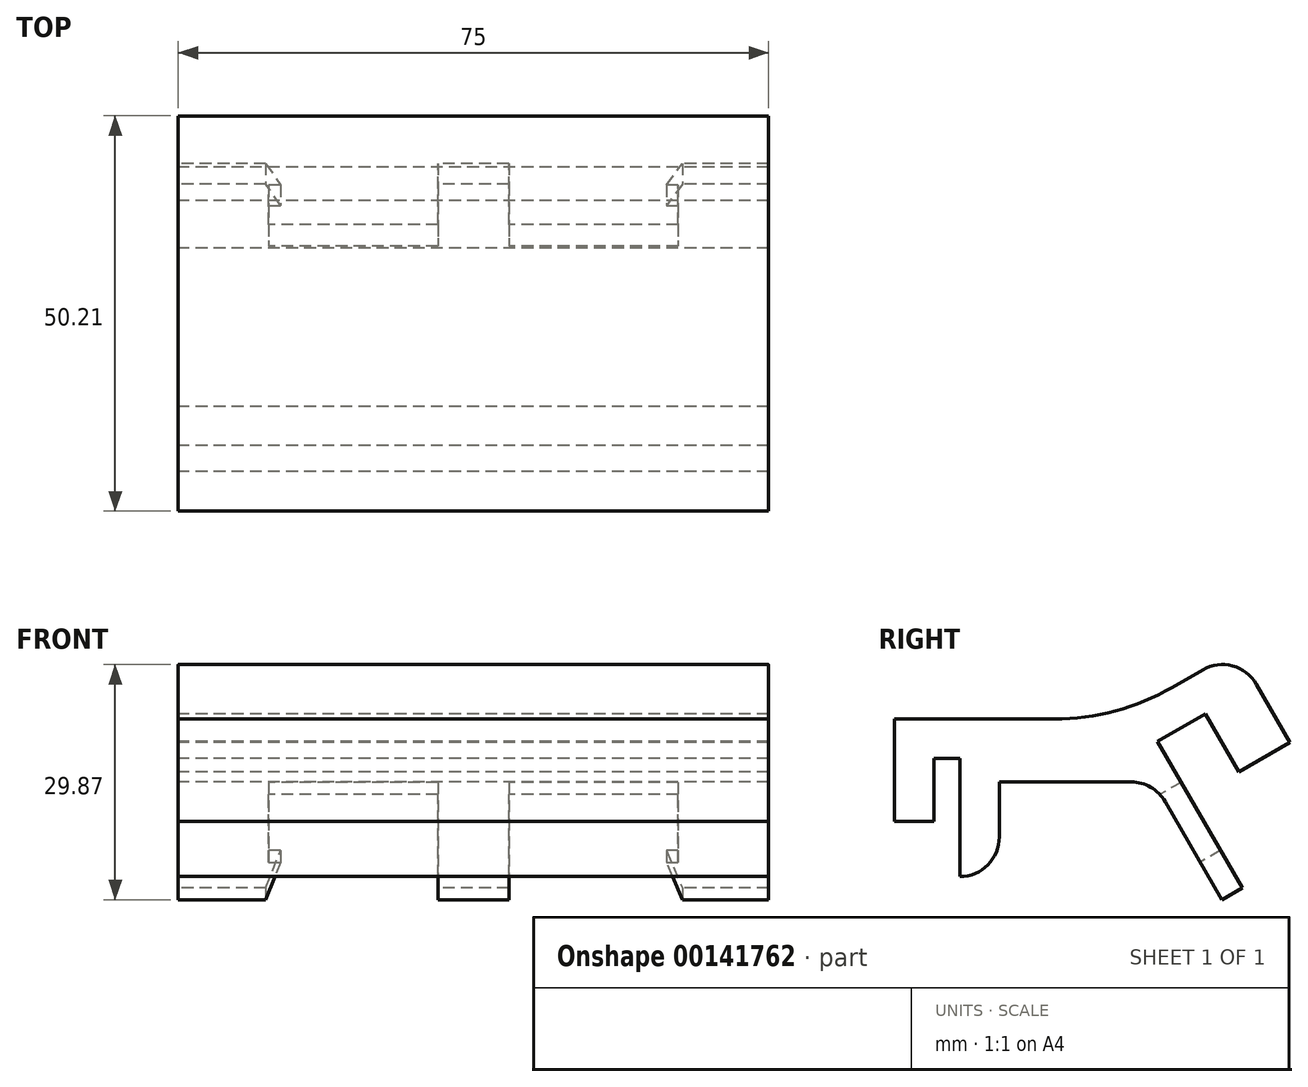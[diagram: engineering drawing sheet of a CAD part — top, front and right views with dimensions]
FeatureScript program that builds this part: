
annotation { "Feature Type Name" : "Feature", "Feature Type Description" : "" }
export const myFeature = defineFeature(function(context is Context, id is Id, definition is map)
    precondition{}
    {
        {
            var Q0;
            Q0=qCreatedBy(makeId("Right.planeOp"),FACE);
            var sketch = newSketch(context, id + "F0", { "sketchPlane" : qUnion([Q0])});
            skLineSegment(sketch, "E0.top", {"start": v(0, 13.5) * mm, "end": v(3, 13.5) * mm});
            skLineSegment(sketch, "E0.left", {"start": v(0, -13) * mm, "end": v(0, 13.5) * mm});
            skLineSegment(sketch, "E0.right", {"start": v(3, -13) * mm, "end": v(3, 8.5) * mm});
            skLineSegment(sketch, "E1.bottom", {"start": v(3, 13.5) * mm, "end": v(10, 13.5) * mm});
            skLineSegment(sketch, "E1.top", {"start": v(3, 8.5) * mm, "end": v(10, 8.5) * mm});
            skLineSegment(sketch, "E2.bottom", {"start": v(10, 13.5) * mm, "end": v(17.5, 13.5) * mm});
            skLineSegment(sketch, "E2.top", {"start": v(10, 0) * mm, "end": v(17.5, 0) * mm});
            skLineSegment(sketch, "E2.left", {"start": v(10, 8.5) * mm, "end": v(10, 0) * mm});
            skLineSegment(sketch, "E2.right", {"start": v(17.5, 13.5) * mm, "end": v(17.5, 0) * mm});
            skLineSegment(sketch, "E3.bottom", {"start": v(-42.45, 43.54) * mm, "end": v(-37.45, 43.54) * mm});
            skLineSegment(sketch, "E3.top", {"start": v(-42.45, 30.54) * mm, "end": v(-37.45, 30.54) * mm});
            skLineSegment(sketch, "E3.left", {"start": v(-42.45, 43.54) * mm, "end": v(-42.45, 30.54) * mm});
            skLineSegment(sketch, "E3.right", {"start": v(-37.45, 43.54) * mm, "end": v(-37.45, 30.54) * mm});
            skLineSegment(sketch, "E4.bottom", {"start": v(-37.45, 43.54) * mm, "end": v(-34.15, 43.54) * mm});
            skLineSegment(sketch, "E4.top", {"start": v(-37.45, 38.54) * mm, "end": v(-34.15, 38.54) * mm});
            skLineSegment(sketch, "E4.left", {"start": v(-37.45, 43.54) * mm, "end": v(-37.45, 38.54) * mm});
            skLineSegment(sketch, "E4.right", {"start": v(-34.15, 43.54) * mm, "end": v(-34.15, 38.54) * mm});
            skLineSegment(sketch, "E5.bottom", {"start": v(-34.15, 43.54) * mm, "end": v(-29.15, 43.54) * mm});
            skLineSegment(sketch, "E5.top", {"start": v(-34.15, 23.54) * mm, "end": v(-29.15, 23.54) * mm});
            skLineSegment(sketch, "E5.left", {"start": v(-34.15, 43.54) * mm, "end": v(-34.15, 23.54) * mm});
            skLineSegment(sketch, "E5.right", {"start": v(-29.15, 43.54) * mm, "end": v(-29.15, 23.54) * mm});
            skLineSegment(sketch, "E6", {"start": v(0, -13) * mm, "end": v(3, -13) * mm});
            skSolve(sketch);
        }
        {
            var Q0;
            Q0=makeQuery(id+"F0.imprint","IMPRINT",FACE,{"disambiguationData":[TD([[makeQuery(id+"F0.imprint","IMPRINT",EDGE,{"derivedFrom":sQuery(id+"F0.wireOp",EDGE,"E0.top")}),-1.0]])]});
            extrude(context, id + "F1", {"entities" : qUnion([Q0]), "depth" : 75 * mm});
        }
        {
            var Q0;
            Q0=qCreatedBy(makeId("Right.planeOp"),FACE);
            var sketch = newSketch(context, id + "F2", { "sketchPlane" : qUnion([Q0])});
            skLineSegment(sketch, "E7.bottom", {"start": v(-28.3, 13.5) * mm, "end": v(-23.3, 13.5) * mm});
            skLineSegment(sketch, "E7.top", {"start": v(-28.3, 0.5) * mm, "end": v(-23.3, 0.5) * mm});
            skLineSegment(sketch, "E7.left", {"start": v(-28.3, 13.5) * mm, "end": v(-28.3, 0.5) * mm});
            skLineSegment(sketch, "E7.right", {"start": v(-23.3, 13.5) * mm, "end": v(-23.3, 0.5) * mm});
            skLineSegment(sketch, "E8.bottom", {"start": v(-23.3, 13.5) * mm, "end": v(-20, 13.5) * mm});
            skLineSegment(sketch, "E8.top", {"start": v(-23.3, 8.5) * mm, "end": v(-20, 8.5) * mm});
            skLineSegment(sketch, "E8.left", {"start": v(-23.3, 13.5) * mm, "end": v(-23.3, 8.5) * mm});
            skLineSegment(sketch, "E8.right", {"start": v(-20, 13.5) * mm, "end": v(-20, 8.5) * mm});
            skLineSegment(sketch, "E9.bottom", {"start": v(-20, 13.5) * mm, "end": v(-15, 13.5) * mm});
            skLineSegment(sketch, "E9.top", {"start": v(-20, -6.5) * mm, "end": v(-15, -6.5) * mm});
            skLineSegment(sketch, "E9.left", {"start": v(-20, 13.5) * mm, "end": v(-20, -6.5) * mm});
            skLineSegment(sketch, "E9.right", {"start": v(-15, 13.5) * mm, "end": v(-15, -6.5) * mm});
            skSolve(sketch);
        }
        {
            var Q0;
            Q0 = qSketchRegion(id + "F2", true);
            extrude(context, id + "F3", {"entities" : qUnion([Q0]), "depth" : 75 * mm});
        }
        {
            var Q0;
            Q0=qCreatedBy(makeId("Front.planeOp"),FACE);
            var sketch = newSketch(context, id + "F4", { "sketchPlane" : qUnion([Q0])});
            skLineSegment(sketch, "E10.bottom", {"start": v(11.5, -7.5) * mm, "end": v(13, -7.5) * mm});
            skLineSegment(sketch, "E10.top", {"start": v(11.5, 2.5) * mm, "end": v(33, 2.5) * mm});
            skLineSegment(sketch, "E10.left", {"start": v(11.5, -7.5) * mm, "end": v(11.5, 2.5) * mm});
            skLineSegment(sketch, "E10.right", {"start": v(33, -7.5) * mm, "end": v(33, 2.5) * mm});
            skLineSegment(sketch, "E11.top", {"start": v(42, 2.5) * mm, "end": v(63.5, 2.5) * mm});
            skLineSegment(sketch, "E11.left", {"start": v(42, -7.5) * mm, "end": v(42, 2.5) * mm});
            skLineSegment(sketch, "E11.right", {"start": v(63.5, -7.5) * mm, "end": v(63.5, 2.5) * mm});
            skLineSegment(sketch, "E12", {"start": v(13, -7.5) * mm, "end": v(11.12, -13) * mm});
            skLineSegment(sketch, "E13", {"start": v(11.12, -13) * mm, "end": v(33, -13) * mm});
            skLineSegment(sketch, "E14", {"start": v(33, -13) * mm, "end": v(33, -7.5) * mm});
            skLineSegment(sketch, "E15", {"start": v(42, -7.5) * mm, "end": v(42, -13) * mm});
            skLineSegment(sketch, "E16", {"start": v(42, -13) * mm, "end": v(64.04, -13) * mm});
            skLineSegment(sketch, "E17", {"start": v(64.04, -13) * mm, "end": v(62, -7.5) * mm});
            skLineSegment(sketch, "E18.trimOffspring", {"start": v(62, -7.5) * mm, "end": v(63.5, -7.5) * mm});
            skSolve(sketch);
        }
        {
            var Q0;
            Q0 = qSketchRegion(id + "F4", true);
            extrude(context, id + "F5", {"entities" : qUnion([Q0]), "operationType" : NewBodyOperationType.REMOVE, "endBound" : BoundingType.UP_TO_NEXT, "oppositeDirection" : true, "depth" : 25 * mm});
        }
        {
            var Q0;
            Q0=makeQuery(id+"F1.opExtrude","SWEPT_BODY",BODY,{"disambiguationData":[OSD([sQuery(id+"F0.wireOp",EDGE,"E0.bottom"),sQuery(id+"F0.wireOp",EDGE,"E0.top"),sQuery(id+"F0.wireOp",EDGE,"E0.left"),sQuery(id+"F0.wireOp",EDGE,"E0.right"),sQuery(id+"F0.wireOp",EDGE,"E1.bottom"),sQuery(id+"F0.wireOp",EDGE,"E1.top"),sQuery(id+"F0.wireOp",EDGE,"E2.bottom"),sQuery(id+"F0.wireOp",EDGE,"E2.top"),sQuery(id+"F0.wireOp",EDGE,"E2.left"),sQuery(id+"F0.wireOp",EDGE,"E2.right")])]});
            var Q1;
            Q1=makeQuery(id+"F1.opExtrude","SWEPT_EDGE",EDGE,{"disambiguationData":[OSD([sQuery(id+"F0.wireOp",EDGE,"E0.top"),sQuery(id+"F0.wireOp",EDGE,"E0.left")])]});
            transform(context, id + "F6", {"entities" : qUnion([Q0]), "transformType" : TransformType.ROTATION, "transformAxis" : qUnion([Q1]), "angle" : 30 * degree, "oppositeDirection" : true, "makeCopy" : false});
        }
        {
            var Q0;
            Q0=qCreatedBy(makeId("Right.planeOp"),FACE);
            var sketch = newSketch(context, id + "F7", { "sketchPlane" : qUnion([Q0])});
            skLineSegment(sketch, "E19.bottom", {"start": v(-15, 13.5) * mm, "end": v(0, 13.5) * mm});
            skLineSegment(sketch, "E19.top", {"start": v(-15, 5.5) * mm, "end": v(0, 5.5) * mm});
            skLineSegment(sketch, "E19.left", {"start": v(-15, 13.5) * mm, "end": v(-15, 5.5) * mm});
            skLineSegment(sketch, "E19.right", {"start": v(0, 13.5) * mm, "end": v(0, 5.5) * mm});
            skLineSegment(sketch, "E20", {"start": v(0, 5.5) * mm, "end": v(5.76, 5.5) * mm});
            skLineSegment(sketch, "E21", {"start": v(5.76, 5.5) * mm, "end": v(0, 13.5) * mm});
            skSolve(sketch);
        }
        {
            var Q0;
            Q0 = qSketchRegion(id + "F7", true);
            extrude(context, id + "F8", {"entities" : qUnion([Q0]), "operationType" : NewBodyOperationType.ADD, "depth" : 75 * mm});
        }
        {
            var Q0;
            Q0=makeQuery(id+"F1.opExtrude","SWEPT_EDGE",EDGE,{"disambiguationData":[OSD([sQuery(id+"F0.wireOp",EDGE,"E2.bottom"),sQuery(id+"F0.wireOp",EDGE,"E2.right")])]});
            fillet(context, id + "F9", {"entities" : qUnion([Q0]), "radius" : 5 * mm, "tangentPropagation" : true, "allowEdgeOverflow" : false});
        }
        {
            var Q0;
            Q0=makeQuery(id+"F8.boolean.opBoolean","INTERSECT",EDGE,{"derivedFrom":[makeQuery(id+"F849vBwktIGQLNj_2.boolean.opBoolean","MERGE",FACE,{"derivedFrom":[makeQuery(id+"F1.opExtrude","SWEPT_FACE",FACE,{"disambiguationData":[OSD([sQuery(id+"F0.wireOp",EDGE,"E0.left")])]}),makeQuery(id+"F849vBwktIGQLNj_2.opExtrude","SWEPT_FACE",FACE,{"disambiguationData":[OSD([sQuery(id+"FTJV3qW65ImudQ3_2.wireOp",EDGE,"AuYOISqk-ZqJz-c0P1-AVWn-oc1fHgiShesi.left")])]})]}),makeQuery(id+"F8.opExtrude","SWEPT_FACE",FACE,{"disambiguationData":[OSD([sQuery(id+"F7.wireOp",EDGE,"E19.top"),sQuery(id+"F7.wireOp",EDGE,"E20")])]})]});
            var Q1;
            Q1=makeQuery(id+"F8.opExtrude","SWEPT_EDGE",EDGE,{"disambiguationData":[OSD([sQuery(id+"F7.wireOp",EDGE,"E19.top"),sQuery(id+"F7.wireOp",EDGE,"E19.left")])]});
            var Q2;
            Q2=makeQuery(id+"F3.opExtrude","SWEPT_EDGE",EDGE,{"disambiguationData":[OSD([sQuery(id+"F2.wireOp",EDGE,"E9.top"),sQuery(id+"F2.wireOp",EDGE,"E9.right")])]});
            fillet(context, id + "F10", {"entities" : qUnion([Q0, Q1, Q2]), "radius" : 5 * mm, "tangentPropagation" : true, "allowEdgeOverflow" : false});
        }
        {
            var Q0;
            Q0=makeQuery(id+"F8.boolean.opBoolean","MERGE",EDGE,{"derivedFrom":[makeQuery(id+"F1.opExtrude","SWEPT_EDGE",EDGE,{"disambiguationData":[OSD([sQuery(id+"F0.wireOp",EDGE,"E0.top"),sQuery(id+"F0.wireOp",EDGE,"E0.left")])]}),makeQuery(id+"F8.opExtrude","SWEPT_EDGE",EDGE,{"disambiguationData":[OSD([sQuery(id+"F7.wireOp",EDGE,"E19.bottom"),sQuery(id+"F7.wireOp",EDGE,"E19.right"),sQuery(id+"F7.wireOp",EDGE,"E21")])]})]});
            fillet(context, id + "F11", {"entities" : qUnion([Q0]), "radius" : 30 * mm, "tangentPropagation" : true, "allowEdgeOverflow" : false});
        }
    });
